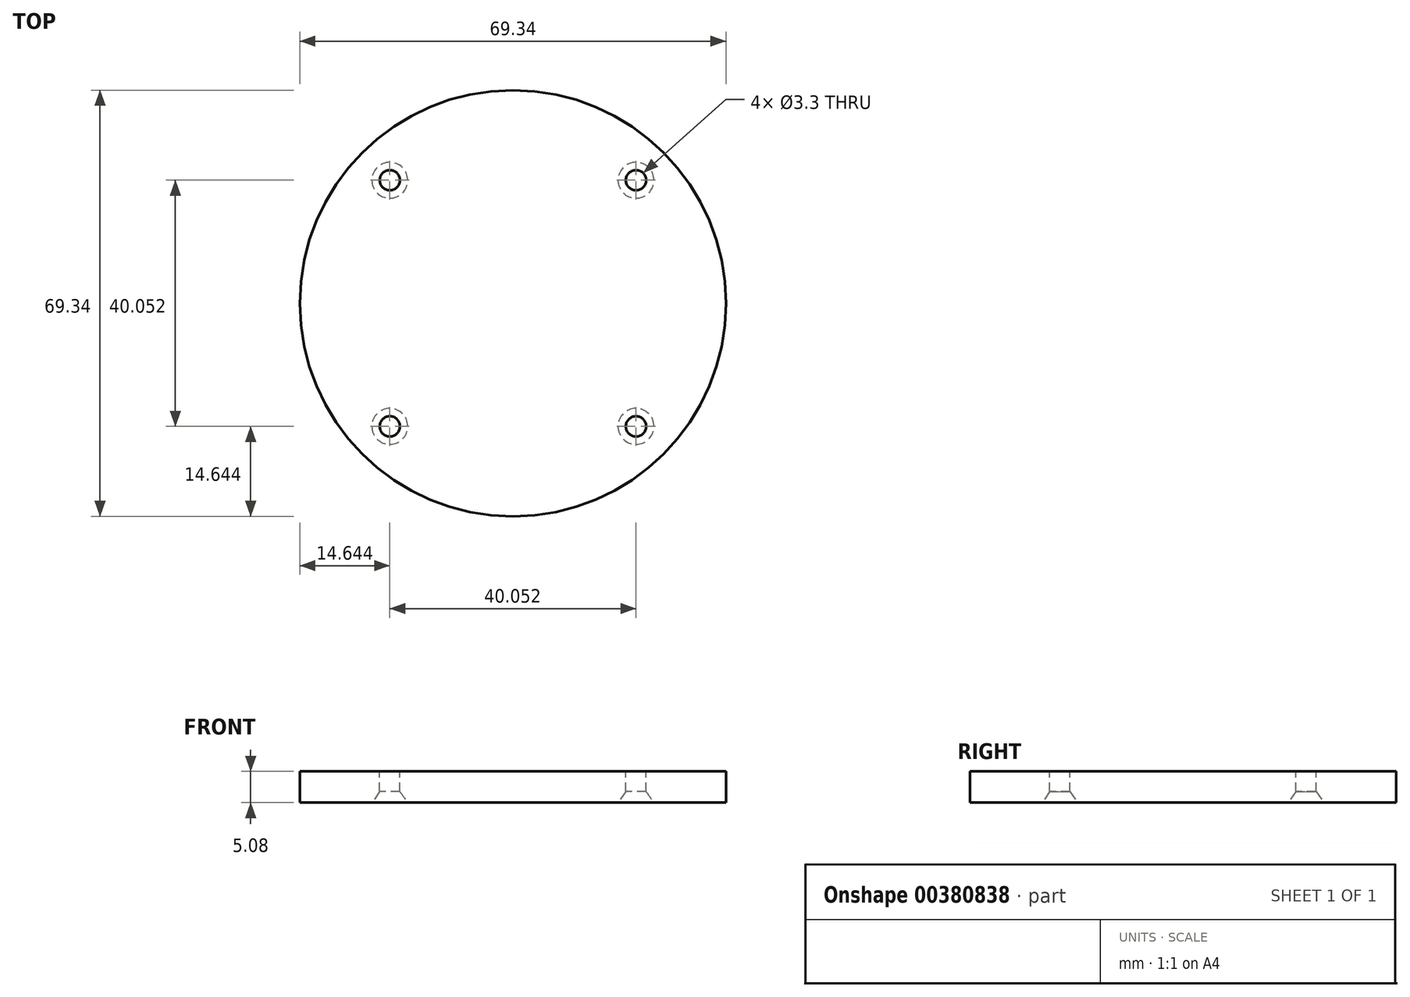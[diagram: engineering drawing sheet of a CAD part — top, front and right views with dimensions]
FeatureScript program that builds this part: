
annotation { "Feature Type Name" : "Feature", "Feature Type Description" : "" }
export const myFeature = defineFeature(function(context is Context, id is Id, definition is map)
    precondition{}
    {
        {
            var Q0;
            Q0=qCreatedBy(makeId("Top.planeOp"),FACE);
            var sketch = newSketch(context, id + "F0", { "sketchPlane" : qUnion([Q0])});
            skCircle(sketch, "E0", {"center": v(0, 0) * mm, "radius": 34.67 * mm});
            skSolve(sketch);
        }
        {
            var Q0;
            Q0 = qSketchRegion(id + "F0", true);
            extrude(context, id + "F1", {"entities" : qUnion([Q0]), "depth" : 5.08 * mm});
        }
        {
            var Q0;
            Q0=makeQuery(id+"F1.opExtrude","CAP_FACE",FACE,{"disambiguationData":[OSD([sQuery(id+"F0.wireOp",EDGE,"E0")])],"isStart":false});
            var sketch = newSketch(context, id + "F2", { "sketchPlane" : qUnion([Q0])});
            skLineSegment(sketch, "E1", {"start": v(0, 0) * mm, "end": v(24.52, 24.52) * mm});
            skLineSegment(sketch, "E2", {"start": v(24.52, 24.52) * mm, "end": v(-24.52, -24.52) * mm});
            skLineSegment(sketch, "E3", {"start": v(-24.52, 24.52) * mm, "end": v(24.52, -24.52) * mm});
            skCircle(sketch, "E4", {"center": v(20.03, 20.03) * mm, "radius": 1.65 * mm});
            skCircle(sketch, "E5.1.0", {"center": v(-20.03, 20.03) * mm, "radius": 1.65 * mm});
            skCircle(sketch, "E5.2.0", {"center": v(-20.03, -20.03) * mm, "radius": 1.65 * mm});
            skCircle(sketch, "E5.3.0", {"center": v(20.03, -20.03) * mm, "radius": 1.65 * mm});
            skPoint(sketch, "E5.center", {"position": v(0, 0) * mm});
            skSolve(sketch);
        }
        {
            var Q0;
            Q0 = qSketchRegion(id + "F2", true);
            extrude(context, id + "F3", {"entities" : qUnion([Q0]), "operationType" : NewBodyOperationType.REMOVE, "oppositeDirection" : true, "depth" : 25.4 * mm});
        }
        {
            var Q0;
            Q0=makeQuery(id+"F3.boolean.opBoolean","INTERSECT",EDGE,{"derivedFrom":[makeQuery(id+"F1.opExtrude","CAP_FACE",FACE,{"disambiguationData":[OSD([sQuery(id+"F0.wireOp",EDGE,"E0")])],"isStart":true}),makeQuery(id+"F3.opExtrude","SWEPT_FACE",FACE,{"disambiguationData":[OSD([sQuery(id+"F2.wireOp",EDGE,"E5.2.0")])]})]});
            var Q1;
            Q1=makeQuery(id+"F3.boolean.opBoolean","INTERSECT",EDGE,{"derivedFrom":[makeQuery(id+"F1.opExtrude","CAP_FACE",FACE,{"disambiguationData":[OSD([sQuery(id+"F0.wireOp",EDGE,"E0")])],"isStart":true}),makeQuery(id+"F3.opExtrude","SWEPT_FACE",FACE,{"disambiguationData":[OSD([sQuery(id+"F2.wireOp",EDGE,"E5.3.0")])]})]});
            var Q2;
            Q2=makeQuery(id+"F3.boolean.opBoolean","INTERSECT",EDGE,{"derivedFrom":[makeQuery(id+"F1.opExtrude","CAP_FACE",FACE,{"disambiguationData":[OSD([sQuery(id+"F0.wireOp",EDGE,"E0")])],"isStart":true}),makeQuery(id+"F3.opExtrude","SWEPT_FACE",FACE,{"disambiguationData":[OSD([sQuery(id+"F2.wireOp",EDGE,"E4")])]})]});
            var Q3;
            Q3=makeQuery(id+"F3.boolean.opBoolean","INTERSECT",EDGE,{"derivedFrom":[makeQuery(id+"F1.opExtrude","CAP_FACE",FACE,{"disambiguationData":[OSD([sQuery(id+"F0.wireOp",EDGE,"E0")])],"isStart":true}),makeQuery(id+"F3.opExtrude","SWEPT_FACE",FACE,{"disambiguationData":[OSD([sQuery(id+"F2.wireOp",EDGE,"E5.1.0")])]})]});
            chamfer(context, id + "F4", {"entities" : qUnion([Q0, Q1, Q2, Q3]), "chamferType" : ChamferType.TWO_OFFSETS, "width1" : 1.27 * mm, "oppositeDirection" : false, "width2" : 1.78 * mm, "tangentPropagation" : true});
        }
    });
